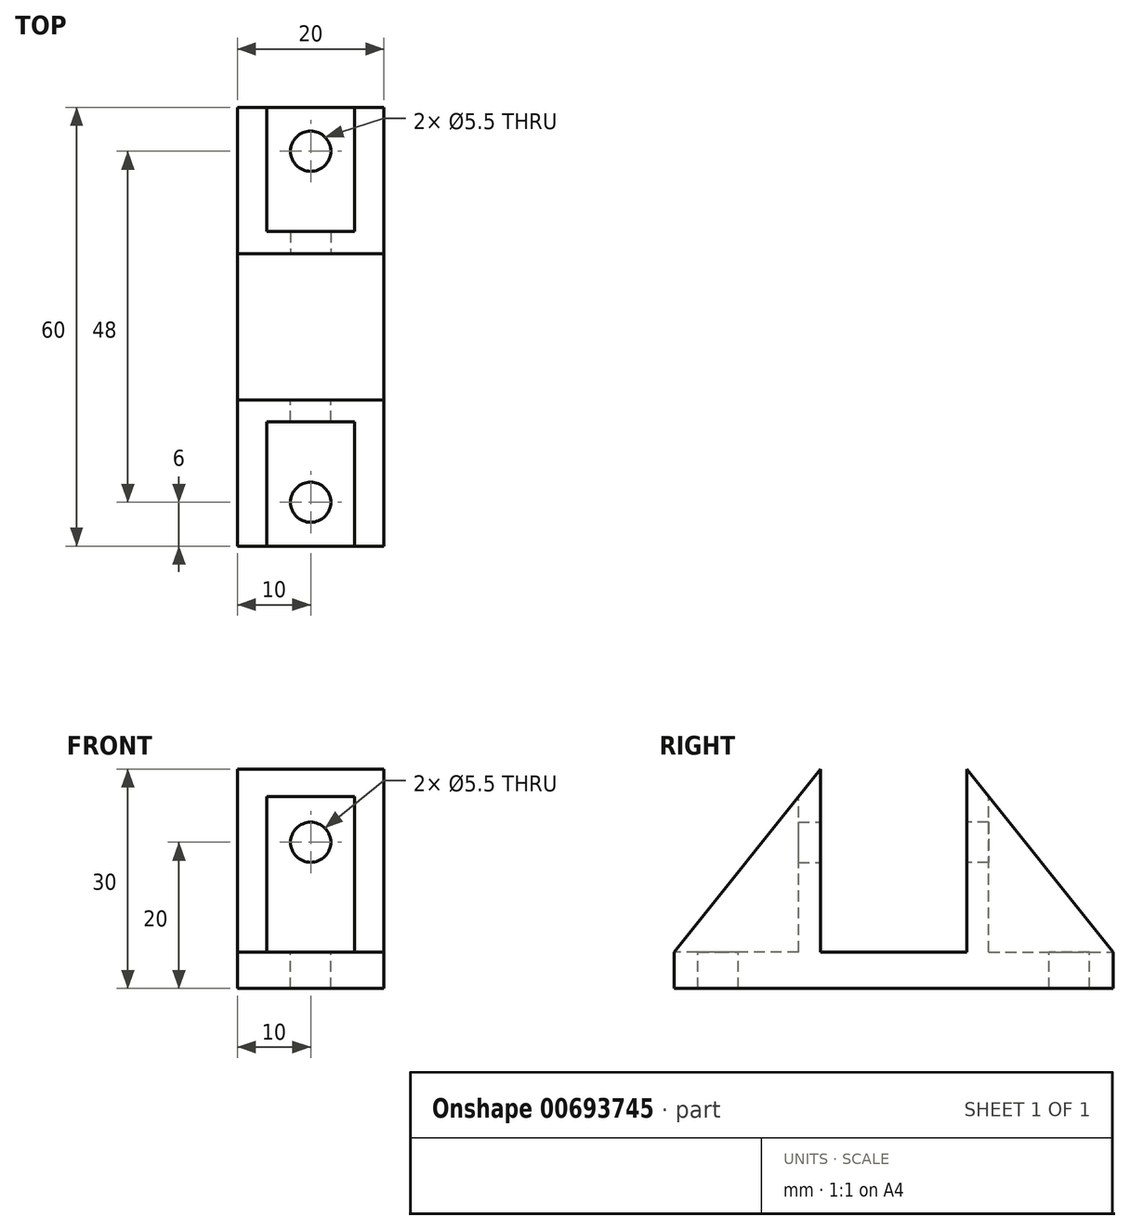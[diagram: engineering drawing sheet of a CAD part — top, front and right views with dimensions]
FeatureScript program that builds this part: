
annotation { "Feature Type Name" : "Feature", "Feature Type Description" : "" }
export const myFeature = defineFeature(function(context is Context, id is Id, definition is map)
    precondition{}
    {
        {
            var Q0;
            Q0=qCreatedBy(makeId("Top.planeOp"),FACE);
            var sketch = newSketch(context, id + "F0", { "sketchPlane" : qUnion([Q0])});
            skLineSegment(sketch, "E0.left", {"start": v(-10, 0) * mm, "end": v(-10, 20) * mm});
            skLineSegment(sketch, "E0.right", {"start": v(10, 0) * mm, "end": v(10, 20) * mm});
            skLineSegment(sketch, "E1.top", {"start": v(-10, 40) * mm, "end": v(10, 40) * mm});
            skLineSegment(sketch, "E1.left", {"start": v(-10, 20) * mm, "end": v(-10, 40) * mm});
            skLineSegment(sketch, "E1.right", {"start": v(10, 20) * mm, "end": v(10, 40) * mm});
            skLineSegment(sketch, "E2.top", {"start": v(-10, -20) * mm, "end": v(10, -20) * mm});
            skLineSegment(sketch, "E2.left", {"start": v(-10, 0) * mm, "end": v(-10, -20) * mm});
            skLineSegment(sketch, "E2.right", {"start": v(10, 0) * mm, "end": v(10, -20) * mm});
            skSolve(sketch);
        }
        {
            var Q0;
            Q0=makeQuery(id+"F0.imprint","IMPRINT",FACE,{"disambiguationData":[TD([[makeQuery(id+"F0.imprint","IMPRINT",EDGE,{"derivedFrom":sQuery(id+"F0.wireOp",EDGE,"E0.left")}),-1.0]])]});
            extrude(context, id + "F1", {"entities" : qUnion([Q0]), "depth" : 30 * mm, "offsetDistance" : 25 * mm});
        }
        {
            var Q0;
            Q0=makeQuery(id+"F1.opExtrude","SWEPT_FACE",FACE,{"disambiguationData":[OSD([sQuery(id+"F0.wireOp",EDGE,"E0.left"),sQuery(id+"F0.wireOp",EDGE,"E1.left"),sQuery(id+"F0.wireOp",EDGE,"E2.left")])]});
            var sketch = newSketch(context, id + "F2", { "sketchPlane" : qUnion([Q0])});
            skLineSegment(sketch, "E3.bottom", {"start": v(-20, 30) * mm, "end": v(0, 30) * mm});
            skLineSegment(sketch, "E3.top", {"start": v(-20, 5) * mm, "end": v(0, 5) * mm});
            skLineSegment(sketch, "E3.left", {"start": v(-20, 30) * mm, "end": v(-20, 5) * mm});
            skLineSegment(sketch, "E3.right", {"start": v(0, 30) * mm, "end": v(0, 5) * mm});
            skLineSegment(sketch, "E4", {"start": v(0, 30) * mm, "end": v(20, 5) * mm});
            skLineSegment(sketch, "E5", {"start": v(-20, 30) * mm, "end": v(-40, 5) * mm});
            skSolve(sketch);
        }
        {
            var Q0;
            {var subQ0=sQuery(id+"F2.wireOp",EDGE,"E5");Q0=makeQuery(id+"F2.imprint","IMPRINT",FACE,{"disambiguationData":[TD([[makeQuery(id+"F2.imprint","IMPRINT",EDGE,{"derivedFrom":subQ0}),-1.0]])]});}
            var Q1;
            Q1=makeQuery(id+"F2.imprint","IMPRINT",FACE,{"disambiguationData":[TD([[makeQuery(id+"F2.imprint","IMPRINT",EDGE,{"derivedFrom":sQuery(id+"F2.wireOp",EDGE,"E3.bottom")}),1.0]])]});
            var Q2;
            {var subQ0=sQuery(id+"F2.wireOp",EDGE,"E4");Q2=makeQuery(id+"F2.imprint","IMPRINT",FACE,{"disambiguationData":[TD([[makeQuery(id+"F2.imprint","IMPRINT",EDGE,{"derivedFrom":subQ0}),1.0]])]});}
            extrude(context, id + "F3", {"entities" : qUnion([Q0, Q1, Q2]), "operationType" : NewBodyOperationType.REMOVE, "oppositeDirection" : true, "depth" : 25 * mm, "offsetDistance" : 25 * mm});
        }
        {
            var Q0;
            Q0=makeQuery(id+"F3.boolean.opBoolean","COPY",FACE,{"derivedFrom":makeQuery(id+"F3.opExtrude","SWEPT_FACE",FACE,{"disambiguationData":[OSD([sQuery(id+"F2.wireOp",EDGE,"E3.right")])]})});
            var sketch = newSketch(context, id + "F4", { "sketchPlane" : qUnion([Q0])});
            skPoint(sketch, "E6", {"position": v(0, 20) * mm});
            skSolve(sketch);
        }
        {
            var Q0;
            Q0=makeQuery(id+"F1.opExtrude","SWEPT_FACE",FACE,{"disambiguationData":[OSD([sQuery(id+"F0.wireOp",EDGE,"E1.top")])]});
            var sketch = newSketch(context, id + "F5", { "sketchPlane" : qUnion([Q0])});
            skLineSegment(sketch, "E7.bottom", {"start": v(6, 5) * mm, "end": v(-6, 5) * mm});
            skLineSegment(sketch, "E7.top", {"start": v(6, 30) * mm, "end": v(-6, 30) * mm});
            skLineSegment(sketch, "E7.left", {"start": v(6, 5) * mm, "end": v(6, 30) * mm});
            skLineSegment(sketch, "E7.right", {"start": v(-6, 5) * mm, "end": v(-6, 30) * mm});
            skSolve(sketch);
        }
        {
            var Q0;
            Q0=makeQuery(id+"F5.imprint","IMPRINT",FACE,{"disambiguationData":[TD([[makeQuery(id+"F5.imprint","IMPRINT",EDGE,{"derivedFrom":sQuery(id+"F5.wireOp",EDGE,"E7.bottom")}),1.0]])]});
            extrude(context, id + "F6", {"entities" : qUnion([Q0]), "operationType" : NewBodyOperationType.REMOVE, "oppositeDirection" : true, "depth" : 17 * mm, "offsetDistance" : 25 * mm});
        }
        {
            var Q0;
            Q0=sQuery(id+"F4.wireOp",VERTEX,"E6");
            var Q1;
            Q1=makeQuery(id+"F1.opExtrude","SWEPT_BODY",BODY,{"disambiguationData":[OSD([sQuery(id+"F0.wireOp",EDGE,"E0.left"),sQuery(id+"F0.wireOp",EDGE,"E0.right"),sQuery(id+"F0.wireOp",EDGE,"E1.top"),sQuery(id+"F0.wireOp",EDGE,"E1.left"),sQuery(id+"F0.wireOp",EDGE,"E1.right"),sQuery(id+"F0.wireOp",EDGE,"E2.top"),sQuery(id+"F0.wireOp",EDGE,"E2.left"),sQuery(id+"F0.wireOp",EDGE,"E2.right")])]});
            hole(context, id + "F7", {"style" : HoleStyle.SIMPLE, "endStyle" : HoleEndStyle.THROUGH, "oppositeDirection" : true, "standardTappedOrClearance" : lookupTablePath({ "standard" : "ISO", "fit" : "Normal", "size" : "M5", "type" : "Clearance" }), "standardBlindInLast" : lookupTablePath({ "fit" : "Standard", "standard" : "ISO", "size" : "M5", "type" : "Clearance" }), "holeDiameter" : 5.5 * mm, "majorDiameter" : 5 * mm, "tappedDepth" : 14.5 * mm, "tapClearance" : 3, "locations" : qUnion([Q0]), "scope" : qUnion([Q1])});
        }
        {
            var Q0;
            Q0=makeQuery(id+"F3.boolean.opBoolean","COPY",FACE,{"derivedFrom":makeQuery(id+"F3.opExtrude","SWEPT_FACE",FACE,{"disambiguationData":[OSD([sQuery(id+"F2.wireOp",EDGE,"E3.left")])]})});
            var sketch = newSketch(context, id + "F8", { "sketchPlane" : qUnion([Q0])});
            skPoint(sketch, "E8", {"position": v(0, 20) * mm});
            skSolve(sketch);
        }
        {
            var Q0;
            Q0=sQuery(id+"F8.wireOp",VERTEX,"E8");
            var Q1;
            Q1=makeQuery(id+"F1.opExtrude","SWEPT_BODY",BODY,{"disambiguationData":[OSD([sQuery(id+"F0.wireOp",EDGE,"E0.left"),sQuery(id+"F0.wireOp",EDGE,"E0.right"),sQuery(id+"F0.wireOp",EDGE,"E1.top"),sQuery(id+"F0.wireOp",EDGE,"E1.left"),sQuery(id+"F0.wireOp",EDGE,"E1.right"),sQuery(id+"F0.wireOp",EDGE,"E2.top"),sQuery(id+"F0.wireOp",EDGE,"E2.left"),sQuery(id+"F0.wireOp",EDGE,"E2.right")])]});
            hole(context, id + "F9", {"style" : HoleStyle.SIMPLE, "endStyle" : HoleEndStyle.THROUGH, "oppositeDirection" : true, "standardTappedOrClearance" : lookupTablePath({ "standard" : "ISO", "fit" : "Normal", "size" : "M5", "type" : "Clearance" }), "standardBlindInLast" : lookupTablePath({ "fit" : "Standard", "standard" : "ISO", "size" : "M5", "type" : "Clearance" }), "holeDiameter" : 5.5 * mm, "majorDiameter" : 5 * mm, "tappedDepth" : 14.5 * mm, "tapClearance" : 3, "locations" : qUnion([Q0]), "scope" : qUnion([Q1])});
        }
        {
            var Q0;
            Q0=makeQuery(id+"F1.opExtrude","SWEPT_FACE",FACE,{"disambiguationData":[OSD([sQuery(id+"F0.wireOp",EDGE,"E2.top")])]});
            var sketch = newSketch(context, id + "F10", { "sketchPlane" : qUnion([Q0])});
            skLineSegment(sketch, "E9.bottom", {"start": v(6, 5) * mm, "end": v(-6, 5) * mm});
            skLineSegment(sketch, "E9.top", {"start": v(6, 30) * mm, "end": v(-6, 30) * mm});
            skLineSegment(sketch, "E9.left", {"start": v(6, 5) * mm, "end": v(6, 30) * mm});
            skLineSegment(sketch, "E9.right", {"start": v(-6, 5) * mm, "end": v(-6, 30) * mm});
            skSolve(sketch);
        }
        {
            var Q0;
            Q0=makeQuery(id+"F10.imprint","IMPRINT",FACE,{"disambiguationData":[TD([[makeQuery(id+"F10.imprint","IMPRINT",EDGE,{"derivedFrom":sQuery(id+"F10.wireOp",EDGE,"E9.bottom")}),-1.0]])]});
            extrude(context, id + "F11", {"entities" : qUnion([Q0]), "operationType" : NewBodyOperationType.REMOVE, "oppositeDirection" : true, "depth" : 17 * mm, "offsetDistance" : 25 * mm});
        }
        {
            var Q0;
            Q0=makeQuery(id+"F6.boolean.opBoolean","COPY",FACE,{"derivedFrom":makeQuery(id+"F6.opExtrude","SWEPT_FACE",FACE,{"disambiguationData":[OSD([sQuery(id+"F5.wireOp",EDGE,"E7.bottom")])]})});
            var sketch = newSketch(context, id + "F12", { "sketchPlane" : qUnion([Q0])});
            skPoint(sketch, "E10", {"position": v(0, 34) * mm});
            skPoint(sketch, "E11", {"position": v(0, -14) * mm});
            skSolve(sketch);
        }
        {
            var Q0;
            Q0=sQuery(id+"F12.wireOp",VERTEX,"E10");
            var Q1;
            Q1=sQuery(id+"F12.wireOp",VERTEX,"E11");
            var Q2;
            Q2=makeQuery(id+"F1.opExtrude","SWEPT_BODY",BODY,{"disambiguationData":[OSD([sQuery(id+"F0.wireOp",EDGE,"E0.left"),sQuery(id+"F0.wireOp",EDGE,"E0.right"),sQuery(id+"F0.wireOp",EDGE,"E1.top"),sQuery(id+"F0.wireOp",EDGE,"E1.left"),sQuery(id+"F0.wireOp",EDGE,"E1.right"),sQuery(id+"F0.wireOp",EDGE,"E2.top"),sQuery(id+"F0.wireOp",EDGE,"E2.left"),sQuery(id+"F0.wireOp",EDGE,"E2.right")])]});
            hole(context, id + "F13", {"style" : HoleStyle.SIMPLE, "endStyle" : HoleEndStyle.THROUGH, "standardTappedOrClearance" : lookupTablePath({ "standard" : "ISO", "fit" : "Normal", "size" : "M5", "type" : "Clearance" }), "standardBlindInLast" : lookupTablePath({ "fit" : "Standard", "standard" : "ISO", "size" : "M5", "type" : "Clearance" }), "holeDiameter" : 5.5 * mm, "majorDiameter" : 5 * mm, "tappedDepth" : 14.5 * mm, "tapClearance" : 3, "locations" : qUnion([Q0, Q1]), "scope" : qUnion([Q2])});
        }
    });
